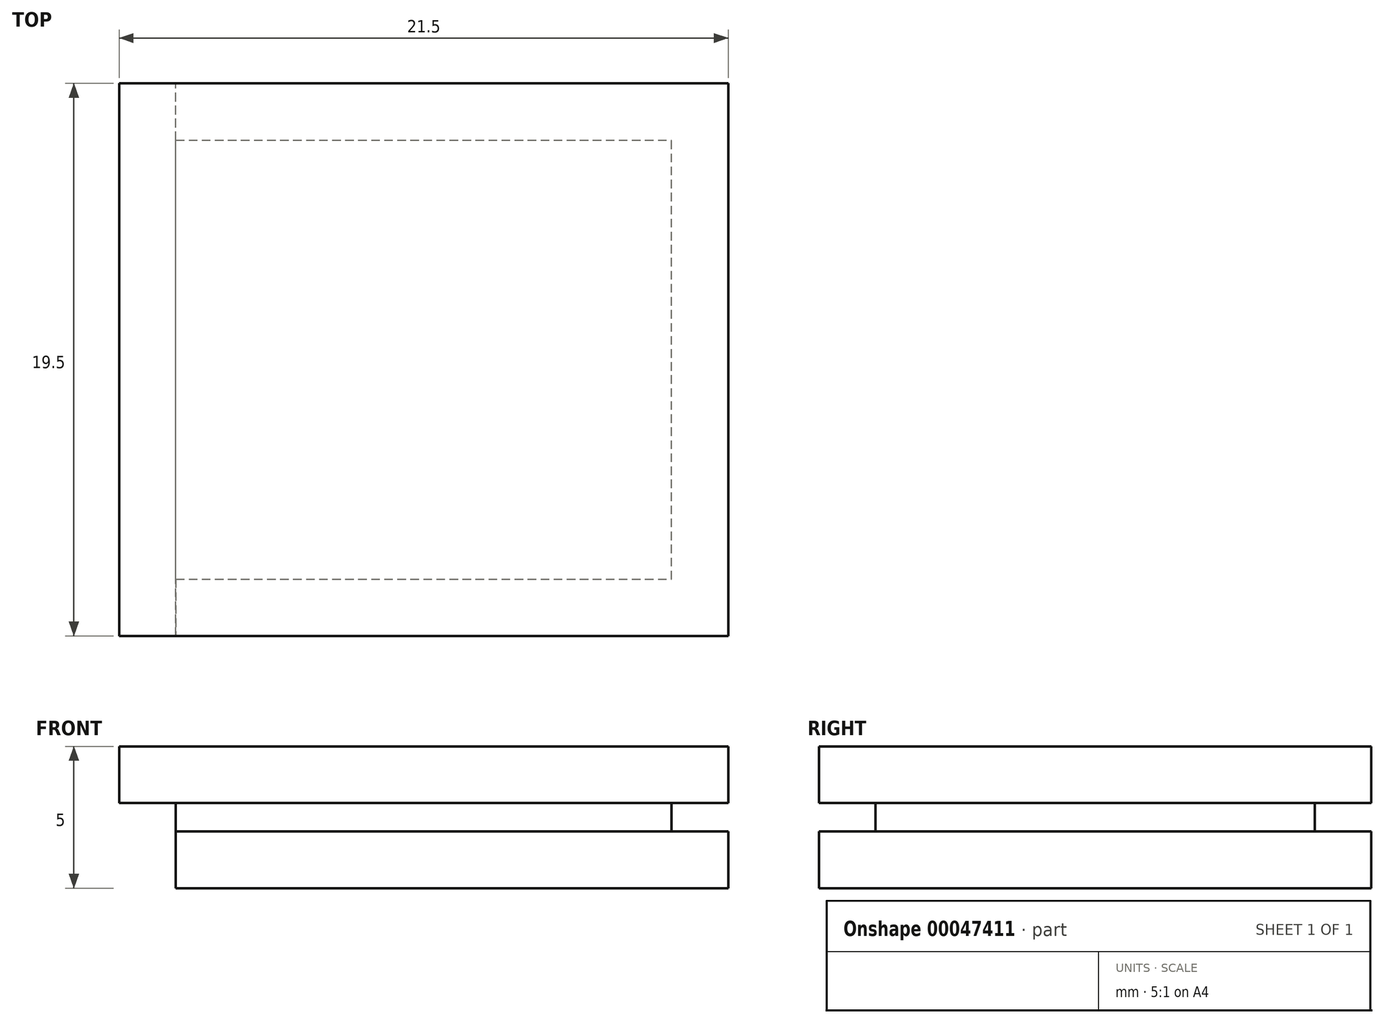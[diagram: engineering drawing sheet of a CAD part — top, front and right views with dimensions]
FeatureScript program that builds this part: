
annotation { "Feature Type Name" : "Feature", "Feature Type Description" : "" }
export const myFeature = defineFeature(function(context is Context, id is Id, definition is map)
    precondition{}
    {
        {
            var Q0;
            Q0=qCreatedBy(makeId("Top.planeOp"),FACE);
            var sketch = newSketch(context, id + "F0", { "sketchPlane" : qUnion([Q0])});
            skLineSegment(sketch, "E0.rect.bottom", {"start": v(-10.75, -9.75) * mm, "end": v(10.75, -9.75) * mm});
            skLineSegment(sketch, "E0.rect.top", {"start": v(-10.75, 9.75) * mm, "end": v(10.75, 9.75) * mm});
            skLineSegment(sketch, "E0.rect.left", {"start": v(-10.75, -9.75) * mm, "end": v(-10.75, 9.75) * mm});
            skLineSegment(sketch, "E0.rect.right", {"start": v(10.75, -9.75) * mm, "end": v(10.75, 9.75) * mm});
            skPoint(sketch, "E0.rect.middle", {"position": v(0, 0) * mm});
            skLineSegment(sketch, "E1.0", {"start": v(-8.75, 7.75) * mm, "end": v(8.75, 7.75) * mm});
            skLineSegment(sketch, "E1.1", {"start": v(-8.75, -7.75) * mm, "end": v(-8.75, 7.75) * mm});
            skLineSegment(sketch, "E1.2", {"start": v(-8.75, -7.75) * mm, "end": v(8.75, -7.75) * mm});
            skLineSegment(sketch, "E1.3", {"start": v(8.75, -7.75) * mm, "end": v(8.75, 7.75) * mm});
            skLineSegment(sketch, "E2", {"start": v(-8.75, 7.75) * mm, "end": v(-8.75, 9.75) * mm});
            skLineSegment(sketch, "E3", {"start": v(-8.75, -7.75) * mm, "end": v(-8.75, -9.75) * mm});
            skSolve(sketch);
        }
        {
            var Q0;
            {var subQ2=sQuery(id+"F0.wireOp",EDGE,"E0.rect.right");Q0=makeQuery(id+"F0.imprint","IMPRINT",FACE,{"disambiguationData":[TD([[makeQuery(id+"F0.imprint","IMPRINT",EDGE,{"derivedFrom":subQ2}),1.0]])]});}
            var Q1;
            Q1=makeQuery(id+"F0.imprint","IMPRINT",FACE,{"disambiguationData":[TD([[makeQuery(id+"F0.imprint","IMPRINT",EDGE,{"derivedFrom":sQuery(id+"F0.wireOp",EDGE,"E1.0")}),-1.0]])]});
            var Q2;
            {var subQ2=sQuery(id+"F0.wireOp",EDGE,"E0.rect.left");Q2=makeQuery(id+"F0.imprint","IMPRINT",FACE,{"disambiguationData":[TD([[makeQuery(id+"F0.imprint","IMPRINT",EDGE,{"derivedFrom":subQ2}),-1.0]])]});}
            extrude(context, id + "F1", {"entities" : qUnion([Q0, Q1, Q2]), "depth" : 2 * mm});
        }
        {
            var Q0;
            Q0=makeQuery(id+"F0.imprint","IMPRINT",FACE,{"disambiguationData":[TD([[makeQuery(id+"F0.imprint","IMPRINT",EDGE,{"derivedFrom":sQuery(id+"F0.wireOp",EDGE,"E1.0")}),-1.0]])]});
            var Q1;
            {var subQ2=sQuery(id+"F0.wireOp",EDGE,"E0.rect.right");Q1=makeQuery(id+"F0.imprint","IMPRINT",FACE,{"disambiguationData":[TD([[makeQuery(id+"F0.imprint","IMPRINT",EDGE,{"derivedFrom":subQ2}),1.0]])]});}
            extrude(context, id + "F2", {"entities" : qUnion([Q0, Q1]), "operationType" : NewBodyOperationType.ADD, "oppositeDirection" : true, "depth" : 3 * mm});
        }
        {
            var Q0;
            {var subQ2=sQuery(id+"F0.wireOp",EDGE,"E0.rect.right");Q0=makeQuery(id+"F0.imprint","IMPRINT",FACE,{"disambiguationData":[TD([[makeQuery(id+"F0.imprint","IMPRINT",EDGE,{"derivedFrom":subQ2}),1.0]])]});}
            extrude(context, id + "F3", {"entities" : qUnion([Q0]), "operationType" : NewBodyOperationType.REMOVE, "oppositeDirection" : true, "depth" : 1 * mm});
        }
    });
